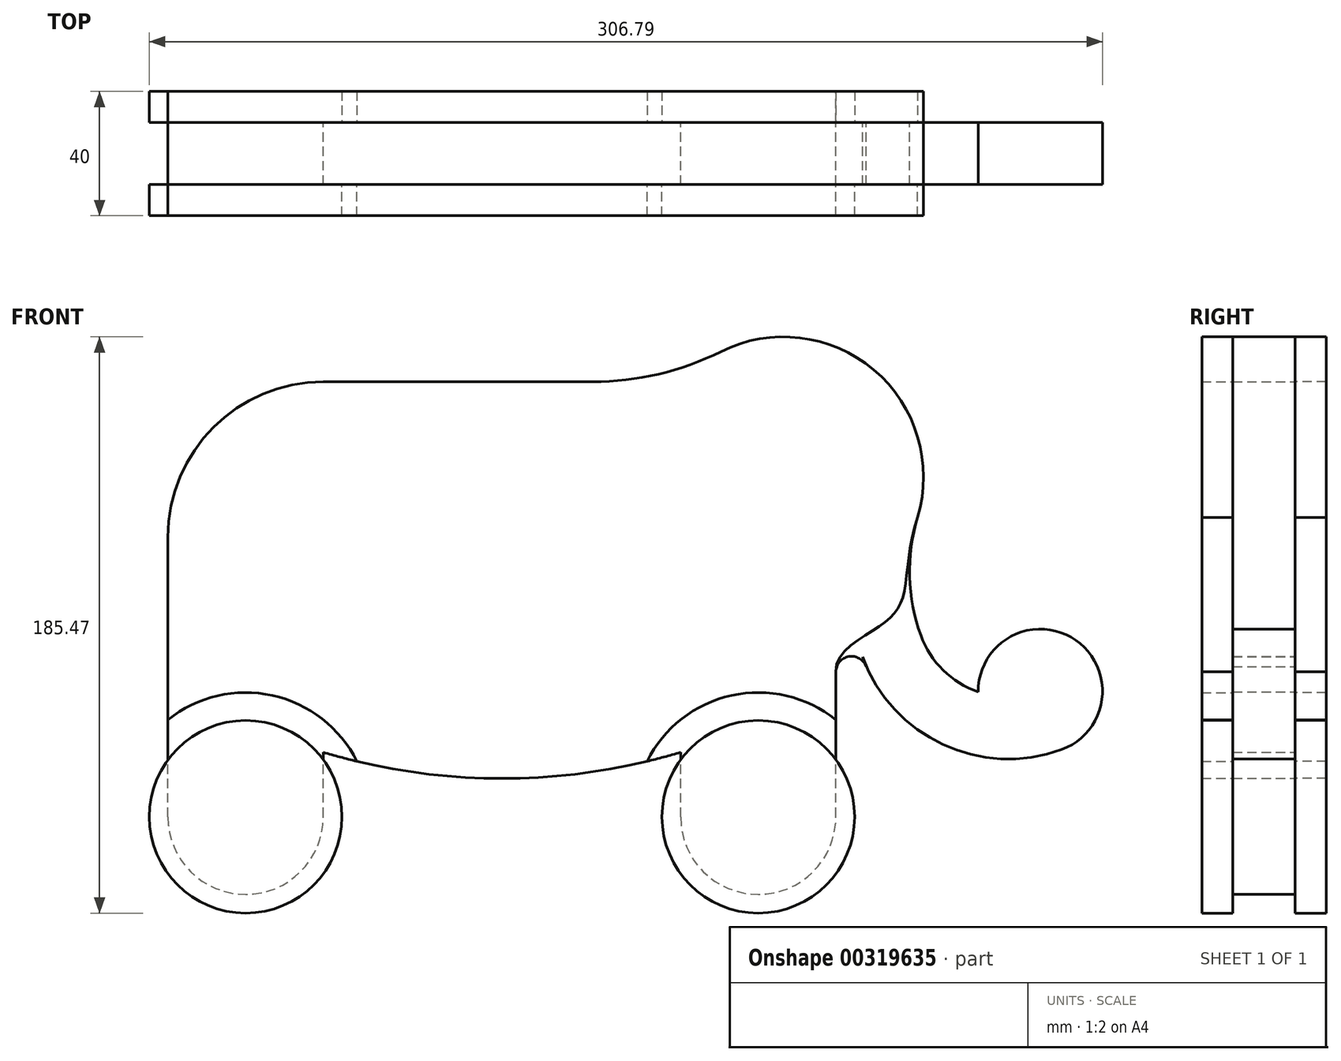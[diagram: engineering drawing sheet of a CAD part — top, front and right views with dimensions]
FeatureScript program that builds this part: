
annotation { "Feature Type Name" : "Feature", "Feature Type Description" : "" }
export const myFeature = defineFeature(function(context is Context, id is Id, definition is map)
    precondition{}
    {
        {
            var Q0;
            Q0=qCreatedBy(makeId("Front.planeOp"),FACE);
            var sketch = newSketch(context, id + "F0", { "sketchPlane" : qUnion([Q0])});
            skCircle(sketch, "E0", {"center": v(30, -5.69) * mm, "radius": 32.5 * mm});
            skCircle(sketch, "E1", {"center": v(-134.99, -5.69) * mm, "radius": 32.5 * mm});
            skCircle(sketch, "E2", {"center": v(-134.99, -5.69) * mm, "radius": 25 * mm});
            skCircle(sketch, "E3", {"center": v(30, -5.69) * mm, "radius": 25 * mm});
            skLineSegment(sketch, "E4", {"start": v(-159.99, -5.69) * mm, "end": v(-159.99, 84.31) * mm});
            skLineSegment(sketch, "E5", {"start": v(-109.99, -5.69) * mm, "end": v(-109.99, 15.08) * mm});
            skLineSegment(sketch, "E6", {"start": v(5, -5.69) * mm, "end": v(5, 15.08) * mm});
            skArc(sketch, "E7", {"start": v(-109.99, 15.08) * mm, "mid": v(-52.5, 6.64) * mm, "end": v(5, 15.08) * mm});
            skLineSegment(sketch, "E8", {"start": v(-109.99, 134.31) * mm, "end": v(5, 134.31) * mm});
            skPoint(sketch, "E9.visualSharp", {"position": v(-159.99, 134.31) * mm});
            skArc(sketch, "E9.filletArc", {"start": v(-109.99, 134.31) * mm, "mid": v(-145.34, 119.67) * mm, "end": v(-159.99, 84.31) * mm});
            skLineSegment(sketch, "E10", {"start": v(55, -5.69) * mm, "end": v(55, 40.95) * mm});
            skLineSegment(sketch, "E11", {"start": v(63.55, 45.82) * mm, "end": v(64.7, 42.66) * mm});
            skLineSegment(sketch, "E12", {"start": v(127.64, 15.94) * mm, "end": v(127.64, 15.94) * mm});
            skLineSegment(sketch, "E13.0", {"start": v(120.8, 34.73) * mm, "end": v(120.8, 34.73) * mm});
            skLineSegment(sketch, "E13.1", {"start": v(73.8, 76.15) * mm, "end": v(82.35, 52.66) * mm});
            skCircle(sketch, "E14", {"center": v(38.1, 103.7) * mm, "radius": 45.09 * mm});
            skCircle(sketch, "E15", {"center": v(120.8, 34.73) * mm, "radius": 20 * mm});
            skPoint(sketch, "E16.visualSharp", {"position": v(80.65, -1.17) * mm});
            skArc(sketch, "E16.filletArc", {"start": v(63.55, 45.82) * mm, "mid": v(89.4, 17.6) * mm, "end": v(127.64, 15.94) * mm});
            skPoint(sketch, "E17.visualSharp", {"position": v(92.6, 24.47) * mm});
            skArc(sketch, "E17.filletArc", {"start": v(82.35, 52.66) * mm, "mid": v(97.86, 35.73) * mm, "end": v(120.8, 34.73) * mm});
            skPoint(sketch, "E18.visualSharp", {"position": v(55, 69.31) * mm});
            skArc(sketch, "E18.filletArc", {"start": v(64.7, 42.66) * mm, "mid": v(59.14, 45.88) * mm, "end": v(55, 40.95) * mm});
            skArc(sketch, "E19", {"start": v(81.27, 90.7) * mm, "mid": v(78.73, 71.59) * mm, "end": v(82.35, 52.66) * mm});
            skArc(sketch, "E20", {"start": v(-23.33, 134.31) * mm, "mid": v(-2.1, 136.78) * mm, "end": v(17.98, 144.04) * mm});
            skSolve(sketch);
        }
        {
            var Q0;
            {var subQ10=sQuery(id+"F0.wireOp",EDGE,"E7");Q0=makeQuery(id+"F0.imprint","IMPRINT",FACE,{"disambiguationData":[TD([[makeQuery(id+"F0.imprint","IMPRINT",EDGE,{"derivedFrom":subQ10}),1.0]])]});}
            var Q1;
            {var subQ0=sQuery(id+"F0.wireOp",EDGE,"E5");Q1=makeQuery(id+"F0.imprint","IMPRINT",FACE,{"disambiguationData":[TD([[makeQuery(id+"F0.imprint","IMPRINT",EDGE,{"derivedFrom":subQ0}),1.0]])]});}
            var Q2;
            {var subQ0=sQuery(id+"F0.wireOp",EDGE,"E2");var subQ1=makeQuery(id+"F0.imprint","INTERSECT",VERTEX,{"derivedFrom":[subQ0,sQuery(id+"F0.wireOp",EDGE,"E4")]});Q2=makeQuery(id+"F0.imprint","IMPRINT",FACE,{"disambiguationData":[TD([[makeQuery(id+"F0.imprint","IMPRINT",EDGE,{"disambiguationData":[TD([[subQ1,1.0]])],"derivedFrom":subQ0}),1.0]])]});}
            var Q3;
            {var subQ0=sQuery(id+"F0.wireOp",EDGE,"E3");var subQ1=makeQuery(id+"F0.imprint","INTERSECT",VERTEX,{"derivedFrom":[subQ0,sQuery(id+"F0.wireOp",EDGE,"E6")]});Q3=makeQuery(id+"F0.imprint","IMPRINT",FACE,{"disambiguationData":[TD([[makeQuery(id+"F0.imprint","IMPRINT",EDGE,{"disambiguationData":[TD([[subQ1,1.0]])],"derivedFrom":subQ0}),1.0]])]});}
            var Q4;
            {var subQ0=sQuery(id+"F0.wireOp",EDGE,"E6");Q4=makeQuery(id+"F0.imprint","IMPRINT",FACE,{"disambiguationData":[TD([[makeQuery(id+"F0.imprint","IMPRINT",EDGE,{"derivedFrom":subQ0}),-1.0]])]});}
            var Q5;
            {var subQ0=sQuery(id+"F0.wireOp",EDGE,"E14");var subQ1=makeQuery(id+"F0.imprint","INTERSECT",VERTEX,{"derivedFrom":[sQuery(id+"F0.wireOp",EDGE,"E8"),subQ0]});Q5=makeQuery(id+"F0.imprint","IMPRINT",FACE,{"disambiguationData":[TD([[makeQuery(id+"F0.imprint","IMPRINT",EDGE,{"disambiguationData":[TD([[subQ1,1.0]])],"derivedFrom":subQ0}),1.0]])]});}
            var Q6;
            {var subQ0=sQuery(id+"F0.wireOp",EDGE,"E13.1");Q6=makeQuery(id+"F0.imprint","IMPRINT",FACE,{"disambiguationData":[TD([[makeQuery(id+"F0.imprint","IMPRINT",EDGE,{"derivedFrom":subQ0}),1.0]])]});}
            var Q7;
            {var subQ3=sQuery(id+"F0.wireOp",EDGE,"E20");Q7=makeQuery(id+"F0.imprint","IMPRINT",FACE,{"disambiguationData":[TD([[makeQuery(id+"F0.imprint","IMPRINT",EDGE,{"derivedFrom":subQ3}),-1.0]])]});}
            var Q8;
            {var subQ0=sQuery(id+"F0.wireOp",EDGE,"E15");var subQ1=makeQuery(id+"F0.imprint","INTERSECT",VERTEX,{"derivedFrom":[subQ0,sQuery(id+"F0.wireOp",EDGE,"E16.filletArc")]});Q8=makeQuery(id+"F0.imprint","IMPRINT",FACE,{"disambiguationData":[TD([[makeQuery(id+"F0.imprint","IMPRINT",EDGE,{"disambiguationData":[TD([[subQ1,1.0]])],"derivedFrom":subQ0}),1.0]])]});}
            extrude(context, id + "F1", {"entities" : qUnion([Q0, Q1, Q2, Q3, Q4, Q5, Q6, Q7, Q8]), "depth" : 20 * mm, "symmetric" : true});
        }
        {
            var Q0;
            Q0=makeQuery(id+"F1.opExtrude","CAP_FACE",FACE,{"disambiguationData":[OSD([sQuery(id+"F0.wireOp",EDGE,"E2"),sQuery(id+"F0.wireOp",EDGE,"E3"),sQuery(id+"F0.wireOp",EDGE,"E4"),sQuery(id+"F0.wireOp",EDGE,"E5"),sQuery(id+"F0.wireOp",EDGE,"E6"),sQuery(id+"F0.wireOp",EDGE,"E7"),sQuery(id+"F0.wireOp",EDGE,"E8"),sQuery(id+"F0.wireOp",EDGE,"E9.filletArc"),sQuery(id+"F0.wireOp",EDGE,"E10"),sQuery(id+"F0.wireOp",EDGE,"E11"),sQuery(id+"F0.wireOp",EDGE,"E14"),sQuery(id+"F0.wireOp",EDGE,"E15"),sQuery(id+"F0.wireOp",EDGE,"E16.filletArc"),sQuery(id+"F0.wireOp",EDGE,"E17.filletArc"),sQuery(id+"F0.wireOp",EDGE,"E18.filletArc"),sQuery(id+"F0.wireOp",EDGE,"E19"),sQuery(id+"F0.wireOp",EDGE,"E20")])],"isStart":false});
            var sketch = newSketch(context, id + "F2", { "sketchPlane" : qUnion([Q0])});
            skCircle(sketch, "E21", {"center": v(-134.99, -5.69) * mm, "radius": 31 * mm});
            skCircle(sketch, "E22", {"center": v(30, -5.69) * mm, "radius": 31 * mm});
            skSolve(sketch);
        }
        {
            var Q0;
            {var subQ4=makeQuery(id+"F1.opExtrude","CAP_EDGE",EDGE,{"disambiguationData":[OSD([sQuery(id+"F0.wireOp",EDGE,"E2")])],"isStart":false});Q0=makeQuery(id+"F2.imprint","IMPRINT",FACE,{"disambiguationData":[TD([[makeQuery(id+"F2.imprint","IMPRINT",EDGE,{"derivedFrom":subQ4}),-1.0]])]});}
            var Q1;
            {var subQ4=makeQuery(id+"F1.opExtrude","CAP_EDGE",EDGE,{"disambiguationData":[OSD([sQuery(id+"F0.wireOp",EDGE,"E2")])],"isStart":false});Q1=makeQuery(id+"F2.imprint","IMPRINT",FACE,{"disambiguationData":[TD([[makeQuery(id+"F2.imprint","IMPRINT",EDGE,{"derivedFrom":subQ4}),1.0]])]});}
            var Q2;
            {var subQ4=makeQuery(id+"F1.opExtrude","CAP_EDGE",EDGE,{"disambiguationData":[OSD([sQuery(id+"F0.wireOp",EDGE,"E3")])],"isStart":false});Q2=makeQuery(id+"F2.imprint","IMPRINT",FACE,{"disambiguationData":[TD([[makeQuery(id+"F2.imprint","IMPRINT",EDGE,{"derivedFrom":subQ4}),-1.0]])]});}
            var Q3;
            {var subQ4=makeQuery(id+"F1.opExtrude","CAP_EDGE",EDGE,{"disambiguationData":[OSD([sQuery(id+"F0.wireOp",EDGE,"E3")])],"isStart":false});Q3=makeQuery(id+"F2.imprint","IMPRINT",FACE,{"disambiguationData":[TD([[makeQuery(id+"F2.imprint","IMPRINT",EDGE,{"derivedFrom":subQ4}),1.0]])]});}
            extrude(context, id + "F3", {"entities" : qUnion([Q0, Q1, Q2, Q3]), "depth" : 10 * mm});
        }
        {
            var Q0;
            Q0=makeQuery(id+"F3.opExtrude","SWEPT_BODY",BODY,{"disambiguationData":[OSD([sQuery(id+"F2.wireOp",EDGE,"E21")])]});
            var Q1;
            Q1=makeQuery(id+"F3.opExtrude","SWEPT_BODY",BODY,{"disambiguationData":[OSD([sQuery(id+"F2.wireOp",EDGE,"E22")])]});
            var Q2;
            Q2=qCreatedBy(makeId("Front.planeOp"),FACE);
            mirror(context, id + "F4", {"entities" : qUnion([Q0, Q1]), "mirrorPlane" : qUnion([Q2])});
        }
        {
            var Q0;
            Q0=makeQuery(id+"F1.opExtrude","CAP_FACE",FACE,{"disambiguationData":[OSD([sQuery(id+"F0.wireOp",EDGE,"E2"),sQuery(id+"F0.wireOp",EDGE,"E3"),sQuery(id+"F0.wireOp",EDGE,"E4"),sQuery(id+"F0.wireOp",EDGE,"E5"),sQuery(id+"F0.wireOp",EDGE,"E6"),sQuery(id+"F0.wireOp",EDGE,"E7"),sQuery(id+"F0.wireOp",EDGE,"E8"),sQuery(id+"F0.wireOp",EDGE,"E9.filletArc"),sQuery(id+"F0.wireOp",EDGE,"E10"),sQuery(id+"F0.wireOp",EDGE,"E11"),sQuery(id+"F0.wireOp",EDGE,"E14"),sQuery(id+"F0.wireOp",EDGE,"E15"),sQuery(id+"F0.wireOp",EDGE,"E16.filletArc"),sQuery(id+"F0.wireOp",EDGE,"E17.filletArc"),sQuery(id+"F0.wireOp",EDGE,"E18.filletArc"),sQuery(id+"F0.wireOp",EDGE,"E19"),sQuery(id+"F0.wireOp",EDGE,"E20")])],"isStart":false});
            var sketch = newSketch(context, id + "F5", { "sketchPlane" : qUnion([Q0])});
            skArc(sketch, "E23.0.0", {"start": v(17.98, 144.04) * mm, "mid": v(-2.1, 136.78) * mm, "end": v(-23.33, 134.31) * mm});
            skLineSegment(sketch, "E23.0.1", {"start": v(-23.33, 134.31) * mm, "end": v(-109.99, 134.31) * mm});
            skArc(sketch, "E23.0.2", {"start": v(-109.99, 134.31) * mm, "mid": v(-145.34, 119.67) * mm, "end": v(-159.99, 84.31) * mm});
            skLineSegment(sketch, "E23.0.3", {"start": v(-159.99, 84.31) * mm, "end": v(-159.99, -5.69) * mm});
            skArc(sketch, "E23.0.4", {"start": v(-159.99, -5.69) * mm, "mid": v(-134.99, -30.69) * mm, "end": v(-109.99, -5.69) * mm});
            skLineSegment(sketch, "E23.0.5", {"start": v(-109.99, -5.69) * mm, "end": v(-109.99, 15.08) * mm});
            skArc(sketch, "E23.0.6", {"start": v(-109.99, 15.08) * mm, "mid": v(-52.5, 6.64) * mm, "end": v(5, 15.08) * mm});
            skLineSegment(sketch, "E23.0.7", {"start": v(5, 15.08) * mm, "end": v(5, -5.69) * mm});
            skArc(sketch, "E23.0.8", {"start": v(5, -5.69) * mm, "mid": v(30, -30.69) * mm, "end": v(55, -5.69) * mm});
            skLineSegment(sketch, "E23.0.9", {"start": v(55, -5.69) * mm, "end": v(55, 40.95) * mm});
            skArc(sketch, "E23.0.10", {"start": v(55, 40.95) * mm, "mid": v(59.14, 45.88) * mm, "end": v(64.7, 42.66) * mm});
            skLineSegment(sketch, "E23.0.11", {"start": v(64.7, 42.66) * mm, "end": v(63.55, 45.82) * mm});
            skArc(sketch, "E23.0.12", {"start": v(63.55, 45.82) * mm, "mid": v(89.4, 17.6) * mm, "end": v(127.64, 15.94) * mm});
            skArc(sketch, "E23.0.13", {"start": v(127.64, 15.94) * mm, "mid": v(132.2, 51.16) * mm, "end": v(100.8, 34.54) * mm});
            skArc(sketch, "E23.0.14", {"start": v(100.8, 34.54) * mm, "mid": v(89.52, 41.51) * mm, "end": v(82.35, 52.66) * mm});
            skArc(sketch, "E23.0.15", {"start": v(82.35, 52.66) * mm, "mid": v(78.73, 71.59) * mm, "end": v(81.27, 90.7) * mm});
            skArc(sketch, "E23.0.16", {"start": v(81.27, 90.7) * mm, "mid": v(67.16, 138.17) * mm, "end": v(17.98, 144.04) * mm});
            skCircle(sketch, "E24", {"center": v(-134.99, -5.69) * mm, "radius": 40 * mm});
            skCircle(sketch, "E25", {"center": v(30, -5.69) * mm, "radius": 40 * mm});
            skFitSpline(sketch, "E26", {"points": [v(55, 40.95) * mm, v(68.54, 55.35) * mm, v(76.53, 64.93) * mm, v(81.27, 90.7) * mm], "startDerivative": vector(-3.94, 58.47) * mm, "endDerivative": vector(27.25, 80.2) * mm});
            skSolve(sketch);
        }
        {
            var Q0;
            Q0=makeQuery(id+"F5.imprint","IMPRINT",FACE,{"disambiguationData":[TD([[makeQuery(id+"F5.imprint","IMPRINT",EDGE,{"derivedFrom":sQuery(id+"F5.wireOp",EDGE,"E23.0.0")}),-1.0]])]});
            extrude(context, id + "F6", {"entities" : qUnion([Q0]), "depth" : 10 * mm});
        }
        {
            var Q0;
            Q0=makeQuery(id+"F6.opExtrude","SWEPT_BODY",BODY,{"disambiguationData":[OSD([sQuery(id+"F5.wireOp",EDGE,"E23.0.0"),sQuery(id+"F5.wireOp",EDGE,"E23.0.1"),sQuery(id+"F5.wireOp",EDGE,"E23.0.2"),sQuery(id+"F5.wireOp",EDGE,"E23.0.3"),sQuery(id+"F5.wireOp",EDGE,"E23.0.6"),sQuery(id+"F5.wireOp",EDGE,"E23.0.9"),sQuery(id+"F5.wireOp",EDGE,"E23.0.16"),sQuery(id+"F5.wireOp",EDGE,"E24"),sQuery(id+"F5.wireOp",EDGE,"E25"),sQuery(id+"F5.wireOp",EDGE,"E26")])]});
            var Q1;
            Q1=qCreatedBy(makeId("Front.planeOp"),FACE);
            mirror(context, id + "F7", {"entities" : qUnion([Q0]), "mirrorPlane" : qUnion([Q1])});
        }
    });
